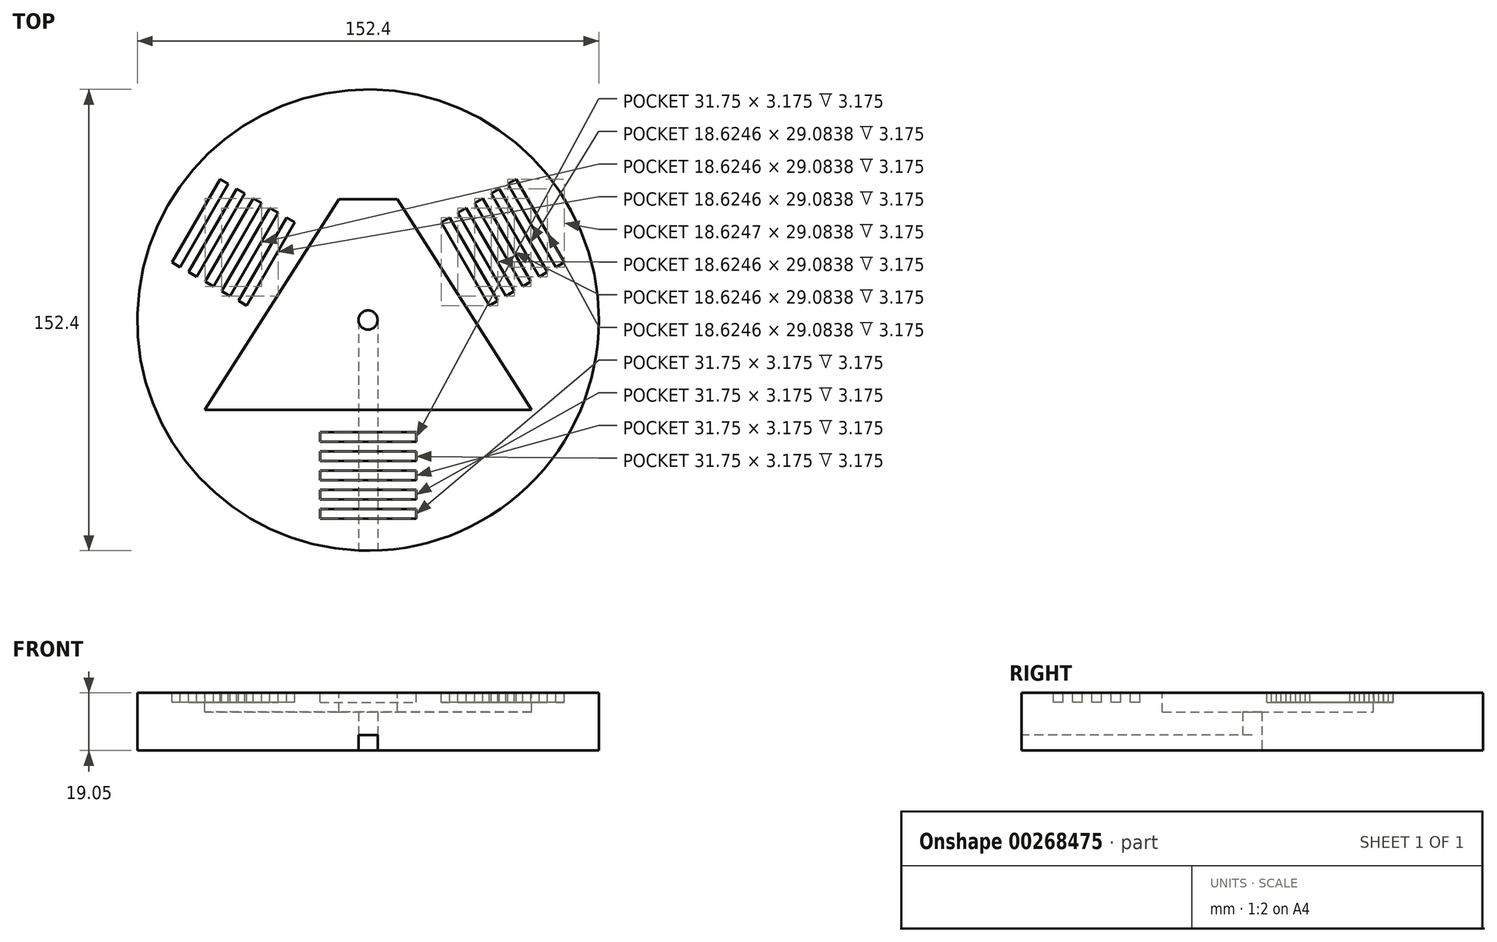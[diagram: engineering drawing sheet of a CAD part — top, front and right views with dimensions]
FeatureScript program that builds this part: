
annotation { "Feature Type Name" : "Feature", "Feature Type Description" : "" }
export const myFeature = defineFeature(function(context is Context, id is Id, definition is map)
    precondition{}
    {
        {
            var Q0;
            Q0=qCreatedBy(makeId("Top.planeOp"),FACE);
            var sketch = newSketch(context, id + "F0", { "sketchPlane" : qUnion([Q0])});
            skCircle(sketch, "E0", {"center": v(0, 0) * mm, "radius": 76.2 * mm});
            skCircle(sketch, "E1", {"center": v(0, 0) * mm, "radius": 3.18 * mm});
            skSolve(sketch);
        }
        {
            var Q0;
            Q0 = qSketchRegion(id + "F0", true);
            extrude(context, id + "F1", {"entities" : qUnion([Q0]), "depth" : 19.05 * mm});
        }
        {
            var Q0;
            Q0=makeQuery(id+"F1.opExtrude","CAP_FACE",FACE,{"disambiguationData":[OSD([sQuery(id+"F0.wireOp",EDGE,"E0"),sQuery(id+"F0.wireOp",EDGE,"E1")])],"isStart":false});
            var sketch = newSketch(context, id + "F2", { "sketchPlane" : qUnion([Q0])});
            skLineSegment(sketch, "E2", {"start": v(-9.65, 39.97) * mm, "end": v(9.65, 39.97) * mm});
            skLineSegment(sketch, "E3", {"start": v(9.65, 39.97) * mm, "end": v(53.98, -29.68) * mm});
            skLineSegment(sketch, "E4", {"start": v(53.98, -29.68) * mm, "end": v(-53.97, -29.68) * mm});
            skLineSegment(sketch, "E5", {"start": v(-53.98, -29.68) * mm, "end": v(-9.65, 39.97) * mm});
            skSolve(sketch);
        }
        {
            var Q0;
            Q0 = qSketchRegion(id + "F2", true);
            extrude(context, id + "F3", {"entities" : qUnion([Q0]), "operationType" : NewBodyOperationType.REMOVE, "oppositeDirection" : true, "depth" : 6.35 * mm});
        }
        {
            var Q0;
            Q0=makeQuery(id+"F1.opExtrude","CAP_FACE",FACE,{"disambiguationData":[OSD([sQuery(id+"F0.wireOp",EDGE,"E0"),sQuery(id+"F0.wireOp",EDGE,"E1")])],"isStart":false});
            var sketch = newSketch(context, id + "F4", { "sketchPlane" : qUnion([Q0])});
            skLineSegment(sketch, "E6", {"start": v(0, -37.07) * mm, "end": v(-15.88, -37.07) * mm, "construction": true});
            skLineSegment(sketch, "E7", {"start": v(-15.88, -37.07) * mm, "end": v(-15.88, -68.82) * mm, "construction": true});
            skLineSegment(sketch, "E8", {"start": v(-15.87, -68.82) * mm, "end": v(15.88, -68.82) * mm, "construction": true});
            skLineSegment(sketch, "E9", {"start": v(15.88, -68.82) * mm, "end": v(15.88, -37.07) * mm, "construction": true});
            skLineSegment(sketch, "E10", {"start": v(15.88, -37.07) * mm, "end": v(0, -37.07) * mm, "construction": true});
            skLineSegment(sketch, "E11.1.0.0", {"start": v(-14.29, -37.07) * mm, "end": v(-14.29, -68.82) * mm, "construction": true});
            skLineSegment(sketch, "E11.2.0.0", {"start": v(-12.7, -37.07) * mm, "end": v(-12.7, -68.82) * mm, "construction": true});
            skLineSegment(sketch, "E11.3.0.0", {"start": v(-11.11, -37.07) * mm, "end": v(-11.11, -68.82) * mm, "construction": true});
            skLineSegment(sketch, "E11.4.0.0", {"start": v(-9.52, -37.07) * mm, "end": v(-9.52, -68.82) * mm, "construction": true});
            skLineSegment(sketch, "E11.5.0.0", {"start": v(-7.94, -37.07) * mm, "end": v(-7.94, -68.82) * mm, "construction": true});
            skLineSegment(sketch, "E11.6.0.0", {"start": v(-6.35, -37.07) * mm, "end": v(-6.35, -68.82) * mm, "construction": true});
            skLineSegment(sketch, "E11.7.0.0", {"start": v(-4.76, -37.07) * mm, "end": v(-4.76, -68.82) * mm, "construction": true});
            skLineSegment(sketch, "E11.8.0.0", {"start": v(-3.17, -37.07) * mm, "end": v(-3.17, -68.82) * mm, "construction": true});
            skLineSegment(sketch, "E11.9.0.0", {"start": v(-1.59, -37.07) * mm, "end": v(-1.59, -68.82) * mm, "construction": true});
            skLineSegment(sketch, "E11.10.0.0", {"start": v(0, -37.07) * mm, "end": v(0, -68.82) * mm, "construction": true});
            skLineSegment(sketch, "E11.11.0.0", {"start": v(1.59, -37.07) * mm, "end": v(1.59, -68.82) * mm, "construction": true});
            skLineSegment(sketch, "E11.12.0.0", {"start": v(3.18, -37.07) * mm, "end": v(3.18, -68.82) * mm, "construction": true});
            skLineSegment(sketch, "E11.13.0.0", {"start": v(4.76, -37.07) * mm, "end": v(4.76, -68.82) * mm, "construction": true});
            skLineSegment(sketch, "E11.14.0.0", {"start": v(6.35, -37.07) * mm, "end": v(6.35, -68.82) * mm, "construction": true});
            skLineSegment(sketch, "E11.15.0.0", {"start": v(7.94, -37.07) * mm, "end": v(7.94, -68.82) * mm, "construction": true});
            skLineSegment(sketch, "E11.16.0.0", {"start": v(9.53, -37.07) * mm, "end": v(9.53, -68.82) * mm, "construction": true});
            skLineSegment(sketch, "E11.17.0.0", {"start": v(11.11, -37.07) * mm, "end": v(11.11, -68.82) * mm, "construction": true});
            skLineSegment(sketch, "E11.18.0.0", {"start": v(12.7, -37.07) * mm, "end": v(12.7, -68.82) * mm, "construction": true});
            skLineSegment(sketch, "E11.19.0.0", {"start": v(14.29, -37.07) * mm, "end": v(14.29, -68.82) * mm, "construction": true});
            skLineSegment(sketch, "E11.direction1", {"start": v(-15.87, -68.82) * mm, "end": v(-14.29, -68.82) * mm, "construction": true});
            skLineSegment(sketch, "E12.0.1.0", {"start": v(-15.87, -67.23) * mm, "end": v(15.88, -67.23) * mm, "construction": true});
            skLineSegment(sketch, "E12.0.2.0", {"start": v(-15.87, -65.64) * mm, "end": v(15.88, -65.64) * mm, "construction": true});
            skLineSegment(sketch, "E12.0.3.0", {"start": v(-15.87, -64.05) * mm, "end": v(15.88, -64.05) * mm, "construction": true});
            skLineSegment(sketch, "E12.0.4.0", {"start": v(-15.87, -62.47) * mm, "end": v(15.88, -62.47) * mm, "construction": true});
            skLineSegment(sketch, "E12.0.5.0", {"start": v(-15.87, -60.88) * mm, "end": v(15.88, -60.88) * mm, "construction": true});
            skLineSegment(sketch, "E12.0.6.0", {"start": v(-15.87, -59.3) * mm, "end": v(15.88, -59.3) * mm, "construction": true});
            skLineSegment(sketch, "E12.0.7.0", {"start": v(-15.87, -57.7) * mm, "end": v(15.88, -57.7) * mm, "construction": true});
            skLineSegment(sketch, "E12.0.8.0", {"start": v(-15.87, -56.12) * mm, "end": v(15.88, -56.12) * mm, "construction": true});
            skLineSegment(sketch, "E12.0.9.0", {"start": v(-15.87, -54.53) * mm, "end": v(15.88, -54.53) * mm, "construction": true});
            skLineSegment(sketch, "E12.0.10.0", {"start": v(-15.87, -52.94) * mm, "end": v(15.88, -52.94) * mm, "construction": true});
            skLineSegment(sketch, "E12.0.11.0", {"start": v(-15.87, -51.35) * mm, "end": v(15.88, -51.35) * mm, "construction": true});
            skLineSegment(sketch, "E12.0.12.0", {"start": v(-15.87, -49.77) * mm, "end": v(15.88, -49.77) * mm, "construction": true});
            skLineSegment(sketch, "E12.0.13.0", {"start": v(-15.87, -48.18) * mm, "end": v(15.88, -48.18) * mm, "construction": true});
            skLineSegment(sketch, "E12.0.14.0", {"start": v(-15.87, -46.6) * mm, "end": v(15.88, -46.6) * mm, "construction": true});
            skLineSegment(sketch, "E12.0.15.0", {"start": v(-15.87, -45) * mm, "end": v(15.88, -45) * mm, "construction": true});
            skLineSegment(sketch, "E12.0.16.0", {"start": v(-15.87, -43.42) * mm, "end": v(15.88, -43.42) * mm, "construction": true});
            skLineSegment(sketch, "E12.0.17.0", {"start": v(-15.87, -41.83) * mm, "end": v(15.88, -41.83) * mm, "construction": true});
            skLineSegment(sketch, "E12.0.18.0", {"start": v(-15.87, -40.24) * mm, "end": v(15.88, -40.24) * mm, "construction": true});
            skLineSegment(sketch, "E12.0.19.0", {"start": v(-15.87, -38.65) * mm, "end": v(15.88, -38.65) * mm, "construction": true});
            skLineSegment(sketch, "E12.direction1", {"start": v(-15.87, -68.82) * mm, "end": v(9.53, -68.82) * mm, "construction": true});
            skLineSegment(sketch, "E12.direction2", {"start": v(-15.87, -68.82) * mm, "end": v(-15.87, -67.23) * mm, "construction": true});
            skLineSegment(sketch, "E13.bottom", {"start": v(-15.88, -37.07) * mm, "end": v(15.88, -37.07) * mm});
            skLineSegment(sketch, "E13.top", {"start": v(-15.87, -40.24) * mm, "end": v(15.88, -40.24) * mm});
            skLineSegment(sketch, "E13.left", {"start": v(-15.87, -37.07) * mm, "end": v(-15.87, -40.24) * mm});
            skLineSegment(sketch, "E13.right", {"start": v(15.88, -37.07) * mm, "end": v(15.88, -40.24) * mm});
            skLineSegment(sketch, "E14.bottom", {"start": v(15.88, -43.42) * mm, "end": v(-15.87, -43.42) * mm});
            skLineSegment(sketch, "E14.top", {"start": v(15.88, -46.6) * mm, "end": v(-15.87, -46.6) * mm});
            skLineSegment(sketch, "E14.left", {"start": v(15.88, -43.42) * mm, "end": v(15.88, -46.6) * mm});
            skLineSegment(sketch, "E14.right", {"start": v(-15.87, -43.42) * mm, "end": v(-15.87, -46.6) * mm});
            skLineSegment(sketch, "E15.bottom", {"start": v(-15.87, -49.77) * mm, "end": v(15.88, -49.77) * mm});
            skLineSegment(sketch, "E15.top", {"start": v(-15.87, -52.94) * mm, "end": v(15.88, -52.94) * mm});
            skLineSegment(sketch, "E15.left", {"start": v(-15.87, -49.77) * mm, "end": v(-15.87, -52.94) * mm});
            skLineSegment(sketch, "E15.right", {"start": v(15.88, -49.77) * mm, "end": v(15.88, -52.94) * mm});
            skLineSegment(sketch, "E16.bottom", {"start": v(15.88, -56.12) * mm, "end": v(-15.87, -56.12) * mm});
            skLineSegment(sketch, "E16.top", {"start": v(15.88, -59.3) * mm, "end": v(-15.87, -59.3) * mm});
            skLineSegment(sketch, "E16.left", {"start": v(15.88, -56.12) * mm, "end": v(15.88, -59.3) * mm});
            skLineSegment(sketch, "E16.right", {"start": v(-15.87, -56.12) * mm, "end": v(-15.87, -59.3) * mm});
            skLineSegment(sketch, "E17.bottom", {"start": v(-15.87, -62.47) * mm, "end": v(15.88, -62.47) * mm});
            skLineSegment(sketch, "E17.top", {"start": v(-15.87, -65.64) * mm, "end": v(15.88, -65.64) * mm});
            skLineSegment(sketch, "E17.left", {"start": v(-15.87, -62.47) * mm, "end": v(-15.87, -65.64) * mm});
            skLineSegment(sketch, "E17.right", {"start": v(15.88, -62.47) * mm, "end": v(15.88, -65.64) * mm});
            skLineSegment(sketch, "E18.1.0", {"start": v(62.04, 17.49) * mm, "end": v(46.16, 44.98) * mm, "construction": true});
            skLineSegment(sketch, "E18.1.1", {"start": v(29.72, 22.66) * mm, "end": v(57.22, 38.54) * mm, "construction": true});
            skLineSegment(sketch, "E18.1.2", {"start": v(56.54, 14.31) * mm, "end": v(40.66, 41.8) * mm, "construction": true});
            skLineSegment(sketch, "E18.1.3", {"start": v(55.16, 13.52) * mm, "end": v(39.29, 41.02) * mm, "construction": true});
            skLineSegment(sketch, "E18.1.4", {"start": v(30.51, 21.29) * mm, "end": v(58, 37.16) * mm, "construction": true});
            skLineSegment(sketch, "E18.1.5", {"start": v(59.29, 15.9) * mm, "end": v(43.41, 43.4) * mm, "construction": true});
            skLineSegment(sketch, "E18.1.6", {"start": v(57.91, 15.1) * mm, "end": v(42.04, 42.6) * mm, "construction": true});
            skLineSegment(sketch, "E18.1.7", {"start": v(63.41, 18.28) * mm, "end": v(47.54, 45.78) * mm, "construction": true});
            skLineSegment(sketch, "E18.1.8", {"start": v(41.41, 5.58) * mm, "end": v(25.54, 33.08) * mm, "construction": true});
            skLineSegment(sketch, "E18.1.9", {"start": v(36.07, 11.66) * mm, "end": v(63.57, 27.54) * mm, "construction": true});
            skLineSegment(sketch, "E18.1.10", {"start": v(28.93, 24.04) * mm, "end": v(56.42, 39.91) * mm, "construction": true});
            skLineSegment(sketch, "E18.1.11", {"start": v(25.75, 29.53) * mm, "end": v(53.25, 45.4) * mm, "construction": true});
            skLineSegment(sketch, "E18.1.12", {"start": v(45.54, 7.96) * mm, "end": v(29.66, 35.46) * mm, "construction": true});
            skLineSegment(sketch, "E18.1.13", {"start": v(39.24, 6.16) * mm, "end": v(66.74, 22.04) * mm, "construction": true});
            skLineSegment(sketch, "E18.1.14", {"start": v(26.54, 28.16) * mm, "end": v(54.04, 44.03) * mm, "construction": true});
            skLineSegment(sketch, "E18.1.15", {"start": v(51.04, 11.14) * mm, "end": v(35.16, 38.63) * mm, "construction": true});
            skLineSegment(sketch, "E18.1.16", {"start": v(28.13, 25.41) * mm, "end": v(55.63, 41.29) * mm, "construction": true});
            skLineSegment(sketch, "E18.1.17", {"start": v(34.48, 14.41) * mm, "end": v(61.98, 30.29) * mm, "construction": true});
            skLineSegment(sketch, "E18.1.18", {"start": v(52.41, 11.93) * mm, "end": v(36.54, 39.43) * mm, "construction": true});
            skLineSegment(sketch, "E18.1.19", {"start": v(46.91, 8.76) * mm, "end": v(31.04, 36.25) * mm, "construction": true});
            skLineSegment(sketch, "E18.1.20", {"start": v(60.66, 16.7) * mm, "end": v(44.79, 44.2) * mm, "construction": true});
            skLineSegment(sketch, "E18.1.21", {"start": v(66.16, 19.87) * mm, "end": v(50.28, 47.37) * mm, "construction": true});
            skLineSegment(sketch, "E18.1.22", {"start": v(44.16, 7.17) * mm, "end": v(28.29, 34.67) * mm, "construction": true});
            skLineSegment(sketch, "E18.1.23", {"start": v(53.79, 12.73) * mm, "end": v(37.91, 40.22) * mm, "construction": true});
            skLineSegment(sketch, "E18.1.24", {"start": v(48.29, 9.55) * mm, "end": v(32.41, 37.05) * mm, "construction": true});
            skLineSegment(sketch, "E18.1.25", {"start": v(32.9, 17.16) * mm, "end": v(60.4, 33.04) * mm, "construction": true});
            skLineSegment(sketch, "E18.1.26", {"start": v(35.28, 13.04) * mm, "end": v(62.77, 28.91) * mm, "construction": true});
            skLineSegment(sketch, "E18.1.27", {"start": v(33.69, 15.79) * mm, "end": v(61.18, 31.66) * mm, "construction": true});
            skLineSegment(sketch, "E18.1.28", {"start": v(32.1, 18.54) * mm, "end": v(59.6, 34.41) * mm, "construction": true});
            skLineSegment(sketch, "E18.1.29", {"start": v(31.3, 19.91) * mm, "end": v(58.8, 35.79) * mm, "construction": true});
            skLineSegment(sketch, "E18.1.30", {"start": v(49.66, 10.34) * mm, "end": v(33.79, 37.84) * mm, "construction": true});
            skLineSegment(sketch, "E18.1.31", {"start": v(36.86, 10.29) * mm, "end": v(64.36, 26.16) * mm, "construction": true});
            skLineSegment(sketch, "E18.1.32", {"start": v(27.34, 26.79) * mm, "end": v(54.83, 42.66) * mm, "construction": true});
            skLineSegment(sketch, "E18.1.33", {"start": v(42.79, 6.38) * mm, "end": v(26.91, 33.87) * mm, "construction": true});
            skLineSegment(sketch, "E18.1.34", {"start": v(37.66, 8.91) * mm, "end": v(65.15, 24.79) * mm, "construction": true});
            skLineSegment(sketch, "E18.1.35", {"start": v(24.96, 30.9) * mm, "end": v(52.45, 46.78) * mm, "construction": true});
            skLineSegment(sketch, "E18.1.36", {"start": v(64.79, 19.08) * mm, "end": v(48.91, 46.57) * mm, "construction": true});
            skLineSegment(sketch, "E18.1.37", {"start": v(38.45, 7.54) * mm, "end": v(65.95, 23.41) * mm, "construction": true});
            skLineSegment(sketch, "E18.1.38", {"start": v(62.04, 17.49) * mm, "end": v(46.16, 44.98) * mm});
            skLineSegment(sketch, "E18.1.39", {"start": v(64.79, 19.08) * mm, "end": v(48.91, 46.57) * mm});
            skLineSegment(sketch, "E18.1.40", {"start": v(42.79, 6.38) * mm, "end": v(26.91, 33.87) * mm});
            skLineSegment(sketch, "E18.1.41", {"start": v(43.41, 43.4) * mm, "end": v(59.29, 15.9) * mm});
            skLineSegment(sketch, "E18.1.42", {"start": v(67.53, 20.66) * mm, "end": v(51.66, 48.16) * mm, "construction": true});
            skLineSegment(sketch, "E18.1.43", {"start": v(29.66, 35.46) * mm, "end": v(45.54, 7.96) * mm});
            skLineSegment(sketch, "E18.1.44", {"start": v(51.04, 11.14) * mm, "end": v(35.16, 38.63) * mm});
            skLineSegment(sketch, "E18.1.45", {"start": v(32.1, 18.54) * mm, "end": v(40.04, 4.79) * mm, "construction": true});
            skLineSegment(sketch, "E18.1.46", {"start": v(53.79, 12.73) * mm, "end": v(37.91, 40.22) * mm});
            skLineSegment(sketch, "E18.1.47", {"start": v(24.16, 32.28) * mm, "end": v(32.1, 18.54) * mm, "construction": true});
            skLineSegment(sketch, "E18.1.48", {"start": v(40.04, 4.79) * mm, "end": v(67.53, 20.66) * mm, "construction": true});
            skLineSegment(sketch, "E18.1.49", {"start": v(40.66, 41.8) * mm, "end": v(56.54, 14.31) * mm});
            skLineSegment(sketch, "E18.1.50", {"start": v(51.66, 48.16) * mm, "end": v(24.16, 32.28) * mm, "construction": true});
            skLineSegment(sketch, "E18.1.51", {"start": v(32.41, 37.05) * mm, "end": v(48.29, 9.55) * mm});
            skLineSegment(sketch, "E18.1.52", {"start": v(67.53, 20.66) * mm, "end": v(54.83, 42.66) * mm, "construction": true});
            skLineSegment(sketch, "E18.1.53", {"start": v(40.66, 41.8) * mm, "end": v(43.41, 43.4) * mm});
            skLineSegment(sketch, "E18.1.54", {"start": v(24.16, 32.28) * mm, "end": v(26.91, 33.87) * mm});
            skLineSegment(sketch, "E18.1.55", {"start": v(62.04, 17.49) * mm, "end": v(64.79, 19.08) * mm});
            skLineSegment(sketch, "E18.1.56", {"start": v(46.16, 44.98) * mm, "end": v(48.91, 46.57) * mm});
            skLineSegment(sketch, "E18.1.57", {"start": v(40.04, 4.79) * mm, "end": v(42.79, 6.38) * mm});
            skLineSegment(sketch, "E18.1.58", {"start": v(40.04, 4.79) * mm, "end": v(24.16, 32.28) * mm});
            skLineSegment(sketch, "E18.1.59", {"start": v(29.66, 35.46) * mm, "end": v(32.41, 37.05) * mm});
            skLineSegment(sketch, "E18.1.60", {"start": v(67.53, 20.66) * mm, "end": v(66.16, 19.87) * mm, "construction": true});
            skLineSegment(sketch, "E18.1.61", {"start": v(56.54, 14.31) * mm, "end": v(59.29, 15.9) * mm});
            skLineSegment(sketch, "E18.1.62", {"start": v(35.16, 38.63) * mm, "end": v(37.91, 40.22) * mm});
            skLineSegment(sketch, "E18.1.63", {"start": v(67.53, 20.66) * mm, "end": v(66.74, 22.04) * mm, "construction": true});
            skLineSegment(sketch, "E18.1.64", {"start": v(45.54, 7.96) * mm, "end": v(48.29, 9.55) * mm});
            skLineSegment(sketch, "E18.1.65", {"start": v(51.04, 11.14) * mm, "end": v(53.79, 12.73) * mm});
            skLineSegment(sketch, "E18.2.0", {"start": v(-46.16, 44.98) * mm, "end": v(-62.04, 17.49) * mm, "construction": true});
            skLineSegment(sketch, "E18.2.1", {"start": v(-34.48, 14.41) * mm, "end": v(-61.98, 30.29) * mm, "construction": true});
            skLineSegment(sketch, "E18.2.2", {"start": v(-40.66, 41.8) * mm, "end": v(-56.54, 14.31) * mm, "construction": true});
            skLineSegment(sketch, "E18.2.3", {"start": v(-39.29, 41.01) * mm, "end": v(-55.16, 13.52) * mm, "construction": true});
            skLineSegment(sketch, "E18.2.4", {"start": v(-33.7, 15.79) * mm, "end": v(-61.19, 31.66) * mm, "construction": true});
            skLineSegment(sketch, "E18.2.5", {"start": v(-43.41, 43.4) * mm, "end": v(-59.29, 15.9) * mm, "construction": true});
            skLineSegment(sketch, "E18.2.6", {"start": v(-42.04, 42.6) * mm, "end": v(-57.91, 15.1) * mm, "construction": true});
            skLineSegment(sketch, "E18.2.7", {"start": v(-47.54, 45.78) * mm, "end": v(-63.41, 18.28) * mm, "construction": true});
            skLineSegment(sketch, "E18.2.8", {"start": v(-25.54, 33.08) * mm, "end": v(-41.42, 5.58) * mm, "construction": true});
            skLineSegment(sketch, "E18.2.9", {"start": v(-28.13, 25.4) * mm, "end": v(-55.63, 41.28) * mm, "construction": true});
            skLineSegment(sketch, "E18.2.10", {"start": v(-35.28, 13.04) * mm, "end": v(-62.77, 28.91) * mm, "construction": true});
            skLineSegment(sketch, "E18.2.11", {"start": v(-38.45, 7.54) * mm, "end": v(-65.95, 23.41) * mm, "construction": true});
            skLineSegment(sketch, "E18.2.12", {"start": v(-29.67, 35.46) * mm, "end": v(-45.54, 7.96) * mm, "construction": true});
            skLineSegment(sketch, "E18.2.13", {"start": v(-24.96, 30.9) * mm, "end": v(-52.46, 46.78) * mm, "construction": true});
            skLineSegment(sketch, "E18.2.14", {"start": v(-37.66, 8.91) * mm, "end": v(-65.16, 24.79) * mm, "construction": true});
            skLineSegment(sketch, "E18.2.15", {"start": v(-35.16, 38.63) * mm, "end": v(-51.04, 11.14) * mm, "construction": true});
            skLineSegment(sketch, "E18.2.16", {"start": v(-36.07, 11.66) * mm, "end": v(-63.57, 27.54) * mm, "construction": true});
            skLineSegment(sketch, "E18.2.17", {"start": v(-29.72, 22.66) * mm, "end": v(-57.22, 38.53) * mm, "construction": true});
            skLineSegment(sketch, "E18.2.18", {"start": v(-36.54, 39.43) * mm, "end": v(-52.41, 11.93) * mm, "construction": true});
            skLineSegment(sketch, "E18.2.19", {"start": v(-31.04, 36.25) * mm, "end": v(-46.91, 8.76) * mm, "construction": true});
            skLineSegment(sketch, "E18.2.20", {"start": v(-44.79, 44.19) * mm, "end": v(-60.66, 16.7) * mm, "construction": true});
            skLineSegment(sketch, "E18.2.21", {"start": v(-50.29, 47.36) * mm, "end": v(-66.16, 19.87) * mm, "construction": true});
            skLineSegment(sketch, "E18.2.22", {"start": v(-28.3, 34.66) * mm, "end": v(-44.17, 7.17) * mm, "construction": true});
            skLineSegment(sketch, "E18.2.23", {"start": v(-37.91, 40.22) * mm, "end": v(-53.79, 12.72) * mm, "construction": true});
            skLineSegment(sketch, "E18.2.24", {"start": v(-32.41, 37.05) * mm, "end": v(-48.29, 9.55) * mm, "construction": true});
            skLineSegment(sketch, "E18.2.25", {"start": v(-31.3, 19.9) * mm, "end": v(-58.8, 35.78) * mm, "construction": true});
            skLineSegment(sketch, "E18.2.26", {"start": v(-28.93, 24.03) * mm, "end": v(-56.42, 39.9) * mm, "construction": true});
            skLineSegment(sketch, "E18.2.27", {"start": v(-30.52, 21.28) * mm, "end": v(-58.01, 37.16) * mm, "construction": true});
            skLineSegment(sketch, "E18.2.28", {"start": v(-32.1, 18.53) * mm, "end": v(-59.6, 34.4) * mm, "construction": true});
            skLineSegment(sketch, "E18.2.29", {"start": v(-32.9, 17.16) * mm, "end": v(-60.4, 33.04) * mm, "construction": true});
            skLineSegment(sketch, "E18.2.30", {"start": v(-33.79, 37.84) * mm, "end": v(-49.66, 10.34) * mm, "construction": true});
            skLineSegment(sketch, "E18.2.31", {"start": v(-27.34, 26.78) * mm, "end": v(-54.84, 42.66) * mm, "construction": true});
            skLineSegment(sketch, "E18.2.32", {"start": v(-36.87, 10.29) * mm, "end": v(-64.36, 26.16) * mm, "construction": true});
            skLineSegment(sketch, "E18.2.33", {"start": v(-26.92, 33.87) * mm, "end": v(-42.8, 6.37) * mm, "construction": true});
            skLineSegment(sketch, "E18.2.34", {"start": v(-26.55, 28.16) * mm, "end": v(-54.04, 44.03) * mm, "construction": true});
            skLineSegment(sketch, "E18.2.35", {"start": v(-39.25, 6.16) * mm, "end": v(-66.74, 22.04) * mm, "construction": true});
            skLineSegment(sketch, "E18.2.36", {"start": v(-48.91, 46.57) * mm, "end": v(-64.79, 19.07) * mm, "construction": true});
            skLineSegment(sketch, "E18.2.37", {"start": v(-25.75, 29.53) * mm, "end": v(-53.25, 45.4) * mm, "construction": true});
            skLineSegment(sketch, "E18.2.38", {"start": v(-46.16, 44.98) * mm, "end": v(-62.04, 17.49) * mm});
            skLineSegment(sketch, "E18.2.39", {"start": v(-48.91, 46.57) * mm, "end": v(-64.79, 19.07) * mm});
            skLineSegment(sketch, "E18.2.40", {"start": v(-26.92, 33.87) * mm, "end": v(-42.8, 6.37) * mm});
            skLineSegment(sketch, "E18.2.41", {"start": v(-59.29, 15.9) * mm, "end": v(-43.41, 43.4) * mm});
            skLineSegment(sketch, "E18.2.42", {"start": v(-51.66, 48.16) * mm, "end": v(-67.54, 20.66) * mm, "construction": true});
            skLineSegment(sketch, "E18.2.43", {"start": v(-45.54, 7.96) * mm, "end": v(-29.67, 35.46) * mm});
            skLineSegment(sketch, "E18.2.44", {"start": v(-35.16, 38.63) * mm, "end": v(-51.04, 11.14) * mm});
            skLineSegment(sketch, "E18.2.45", {"start": v(-32.1, 18.53) * mm, "end": v(-24.17, 32.28) * mm, "construction": true});
            skLineSegment(sketch, "E18.2.46", {"start": v(-37.91, 40.22) * mm, "end": v(-53.79, 12.72) * mm});
            skLineSegment(sketch, "E18.2.47", {"start": v(-40.04, 4.79) * mm, "end": v(-32.1, 18.53) * mm, "construction": true});
            skLineSegment(sketch, "E18.2.48", {"start": v(-24.17, 32.28) * mm, "end": v(-51.66, 48.16) * mm, "construction": true});
            skLineSegment(sketch, "E18.2.49", {"start": v(-56.54, 14.31) * mm, "end": v(-40.66, 41.8) * mm});
            skLineSegment(sketch, "E18.2.50", {"start": v(-67.54, 20.66) * mm, "end": v(-40.04, 4.79) * mm, "construction": true});
            skLineSegment(sketch, "E18.2.51", {"start": v(-48.29, 9.55) * mm, "end": v(-32.41, 37.05) * mm});
            skLineSegment(sketch, "E18.2.52", {"start": v(-51.66, 48.16) * mm, "end": v(-64.36, 26.16) * mm, "construction": true});
            skLineSegment(sketch, "E18.2.53", {"start": v(-56.54, 14.31) * mm, "end": v(-59.29, 15.9) * mm});
            skLineSegment(sketch, "E18.2.54", {"start": v(-40.04, 4.79) * mm, "end": v(-42.8, 6.37) * mm});
            skLineSegment(sketch, "E18.2.55", {"start": v(-46.16, 44.98) * mm, "end": v(-48.91, 46.57) * mm});
            skLineSegment(sketch, "E18.2.56", {"start": v(-62.04, 17.49) * mm, "end": v(-64.79, 19.07) * mm});
            skLineSegment(sketch, "E18.2.57", {"start": v(-24.17, 32.28) * mm, "end": v(-26.92, 33.87) * mm});
            skLineSegment(sketch, "E18.2.58", {"start": v(-24.17, 32.28) * mm, "end": v(-40.04, 4.79) * mm});
            skLineSegment(sketch, "E18.2.59", {"start": v(-45.54, 7.96) * mm, "end": v(-48.29, 9.55) * mm});
            skLineSegment(sketch, "E18.2.60", {"start": v(-51.66, 48.16) * mm, "end": v(-50.29, 47.36) * mm, "construction": true});
            skLineSegment(sketch, "E18.2.61", {"start": v(-40.66, 41.8) * mm, "end": v(-43.41, 43.4) * mm});
            skLineSegment(sketch, "E18.2.62", {"start": v(-51.04, 11.14) * mm, "end": v(-53.79, 12.72) * mm});
            skLineSegment(sketch, "E18.2.63", {"start": v(-51.66, 48.16) * mm, "end": v(-52.46, 46.78) * mm, "construction": true});
            skLineSegment(sketch, "E18.2.64", {"start": v(-29.67, 35.46) * mm, "end": v(-32.41, 37.05) * mm});
            skLineSegment(sketch, "E18.2.65", {"start": v(-35.16, 38.63) * mm, "end": v(-37.91, 40.22) * mm});
            skPoint(sketch, "E18.center", {"position": v(0, 0) * mm});
            skSolve(sketch);
        }
        {
            var Q0;
            Q0 = qSketchRegion(id + "F4", true);
            extrude(context, id + "F5", {"entities" : qUnion([Q0]), "operationType" : NewBodyOperationType.REMOVE, "oppositeDirection" : true, "depth" : 3.17 * mm});
        }
        {
            var Q0;
            Q0=makeQuery(id+"F1.opExtrude","CAP_FACE",FACE,{"disambiguationData":[OSD([sQuery(id+"F0.wireOp",EDGE,"E0"),sQuery(id+"F0.wireOp",EDGE,"E1")])],"isStart":true});
            var sketch = newSketch(context, id + "F6", { "sketchPlane" : qUnion([Q0])});
            skLineSegment(sketch, "E19.bottom", {"start": v(-3.18, 0) * mm, "end": v(3.17, 0) * mm});
            skLineSegment(sketch, "E19.top", {"start": v(-3.18, 79.39) * mm, "end": v(3.17, 79.39) * mm});
            skLineSegment(sketch, "E19.left", {"start": v(-3.18, 0) * mm, "end": v(-3.18, 79.39) * mm});
            skLineSegment(sketch, "E19.right", {"start": v(3.17, 0) * mm, "end": v(3.17, 79.39) * mm});
            skSolve(sketch);
        }
        {
            var Q0;
            Q0 = qSketchRegion(id + "F6", true);
            extrude(context, id + "F7", {"entities" : qUnion([Q0]), "operationType" : NewBodyOperationType.REMOVE, "oppositeDirection" : true, "depth" : 5.08 * mm});
        }
    });
